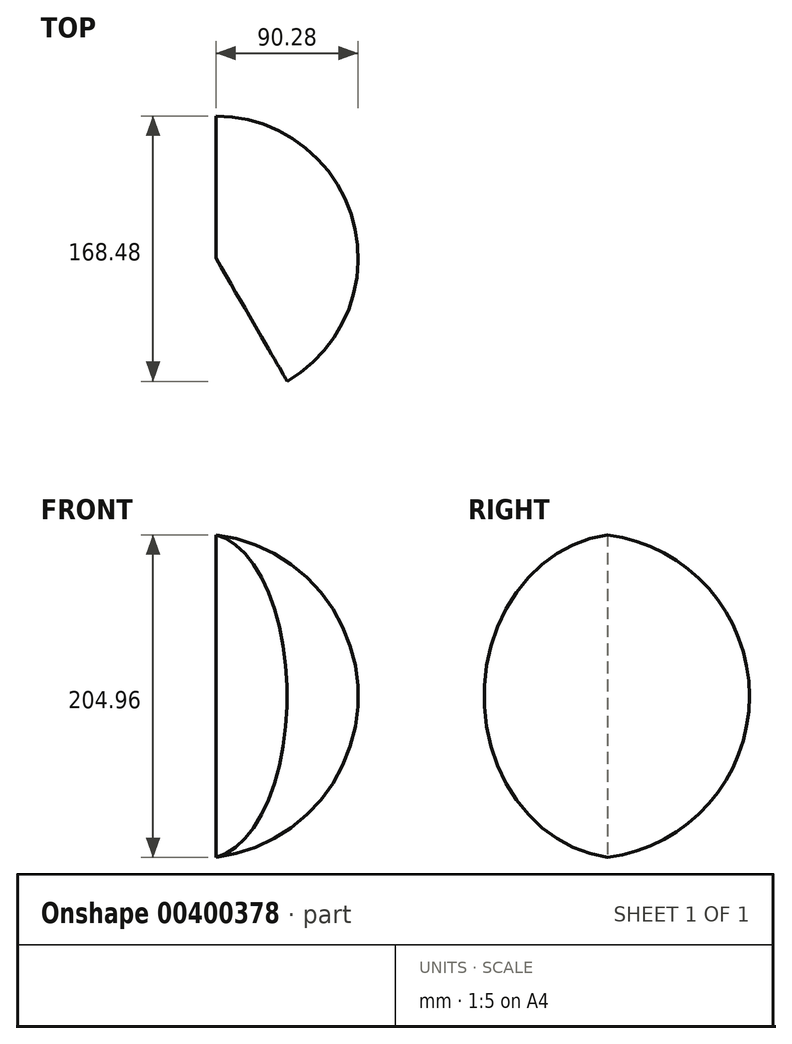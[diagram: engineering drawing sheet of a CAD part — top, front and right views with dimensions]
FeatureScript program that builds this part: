
annotation { "Feature Type Name" : "Feature", "Feature Type Description" : "" }
export const myFeature = defineFeature(function(context is Context, id is Id, definition is map)
    precondition{}
    {
        {
            var Q0;
            Q0=qCreatedBy(makeId("Right.planeOp"),FACE);
            var sketch = newSketch(context, id + "F0", { "sketchPlane" : qUnion([Q0])});
            skLineSegment(sketch, "E0", {"start": v(-27.88, 102.93) * mm, "end": v(-27.88, -102.03) * mm});
            skArc(sketch, "E1", {"start": v(-27.88, -102.03) * mm, "mid": v(62.4, 0.45) * mm, "end": v(-27.88, 102.93) * mm});
            skSolve(sketch);
        }
        {
            var Q0;
            Q0=makeQuery(id+"F0.imprint","IMPRINT",FACE,{"disambiguationData":[TD([[makeQuery(id+"F0.imprint","IMPRINT",EDGE,{"derivedFrom":sQuery(id+"F0.wireOp",EDGE,"E0")}),1.0]])]});
            var Q1;
            Q1=sQuery(id+"F0.wireOp",EDGE,"E0");
            revolve(context, id + "F1", {"entities" : qUnion([Q0]), "axis" : qUnion([Q1]), "revolveType" : RevolveType.ONE_DIRECTION, "angle" : 150 * degree});
        }
    });
